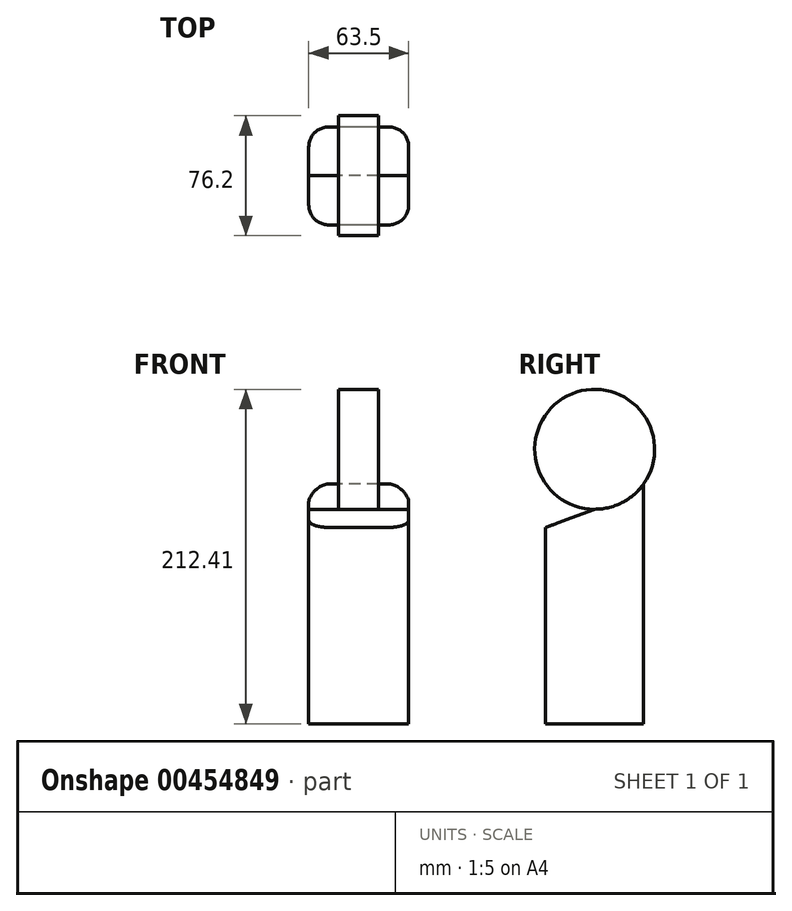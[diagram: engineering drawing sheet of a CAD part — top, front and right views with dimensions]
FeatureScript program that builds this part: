
annotation { "Feature Type Name" : "Feature", "Feature Type Description" : "" }
export const myFeature = defineFeature(function(context is Context, id is Id, definition is map)
    precondition{}
    {
        {
            var Q0;
            Q0=qCreatedBy(makeId("Right.planeOp"),FACE);
            var sketch = newSketch(context, id + "F0", { "sketchPlane" : qUnion([Q0])});
            skCircle(sketch, "E0", {"center": v(0, 0) * mm, "radius": 38.1 * mm});
            skLineSegment(sketch, "E1.bottom", {"start": v(-31.17, -21.9) * mm, "end": v(31.06, -21.9) * mm});
            skLineSegment(sketch, "E1.top", {"start": v(-31.17, -174.3) * mm, "end": v(31.06, -174.3) * mm});
            skLineSegment(sketch, "E1.left", {"start": v(-31.17, -21.9) * mm, "end": v(-31.17, -174.3) * mm});
            skLineSegment(sketch, "E1.right", {"start": v(31.06, -21.9) * mm, "end": v(31.06, -174.3) * mm});
            skLineSegment(sketch, "E2", {"start": v(0, -38.1) * mm, "end": v(-31.17, -49.68) * mm});
            skSolve(sketch);
        }
        {
            var Q0;
            {var subQ0=sQuery(id+"F0.wireOp",EDGE,"E1.bottom");Q0=makeQuery(id+"F0.imprint","IMPRINT",FACE,{"disambiguationData":[TD([[makeQuery(id+"F0.imprint","IMPRINT",EDGE,{"derivedFrom":subQ0}),1.0]])]});}
            var Q1;
            {var subQ1=sQuery(id+"F0.wireOp",EDGE,"E1.top");Q1=makeQuery(id+"F0.imprint","IMPRINT",FACE,{"disambiguationData":[TD([[makeQuery(id+"F0.imprint","IMPRINT",EDGE,{"derivedFrom":subQ1}),1.0]])]});}
            var Q2;
            {var subQ0=sQuery(id+"F0.wireOp",EDGE,"E1.bottom");Q2=makeQuery(id+"F0.imprint","IMPRINT",FACE,{"disambiguationData":[TD([[makeQuery(id+"F0.imprint","IMPRINT",EDGE,{"derivedFrom":subQ0}),-1.0]])]});}
            extrude(context, id + "F1", {"entities" : qUnion([Q0, Q1, Q2]), "endBound" : BoundingType.SYMMETRIC, "depth" : 25.4 * mm, "offsetDistance" : 25.4 * mm});
        }
        {
            var Q0;
            {var subQ4=sQuery(id+"F0.wireOp",EDGE,"E1.top");Q0=makeQuery(id+"F0.imprint","IMPRINT",FACE,{"disambiguationData":[TD([[makeQuery(id+"F0.imprint","IMPRINT",EDGE,{"derivedFrom":subQ4}),1.0]])]});}
            extrude(context, id + "F2", {"entities" : qUnion([Q0]), "operationType" : NewBodyOperationType.ADD, "endBound" : BoundingType.SYMMETRIC, "depth" : 63.5 * mm, "offsetDistance" : 25.4 * mm});
        }
        {
            var Q0;
            Q0=makeQuery(id+"F2.opExtrude","CAP_EDGE",EDGE,{"disambiguationData":[OSD([sQuery(id+"F0.wireOp",EDGE,"E1.left")])],"isStart":false});
            var Q1;
            Q1=makeQuery(id+"F2.opExtrude","CAP_EDGE",EDGE,{"disambiguationData":[OSD([sQuery(id+"F0.wireOp",EDGE,"E1.right")])],"isStart":false});
            var Q2;
            Q2=makeQuery(id+"F2.opExtrude","CAP_EDGE",EDGE,{"disambiguationData":[OSD([sQuery(id+"F0.wireOp",EDGE,"E1.left")])],"isStart":true});
            var Q3;
            Q3=makeQuery(id+"F2.opExtrude","CAP_EDGE",EDGE,{"disambiguationData":[OSD([sQuery(id+"F0.wireOp",EDGE,"E1.right")])],"isStart":true});
            fillet(context, id + "F3", {"entities" : qUnion([Q0, Q1, Q2, Q3]), "radius" : 12.7 * mm, "tangentPropagation" : true, "allowEdgeOverflow" : false});
        }
    });
